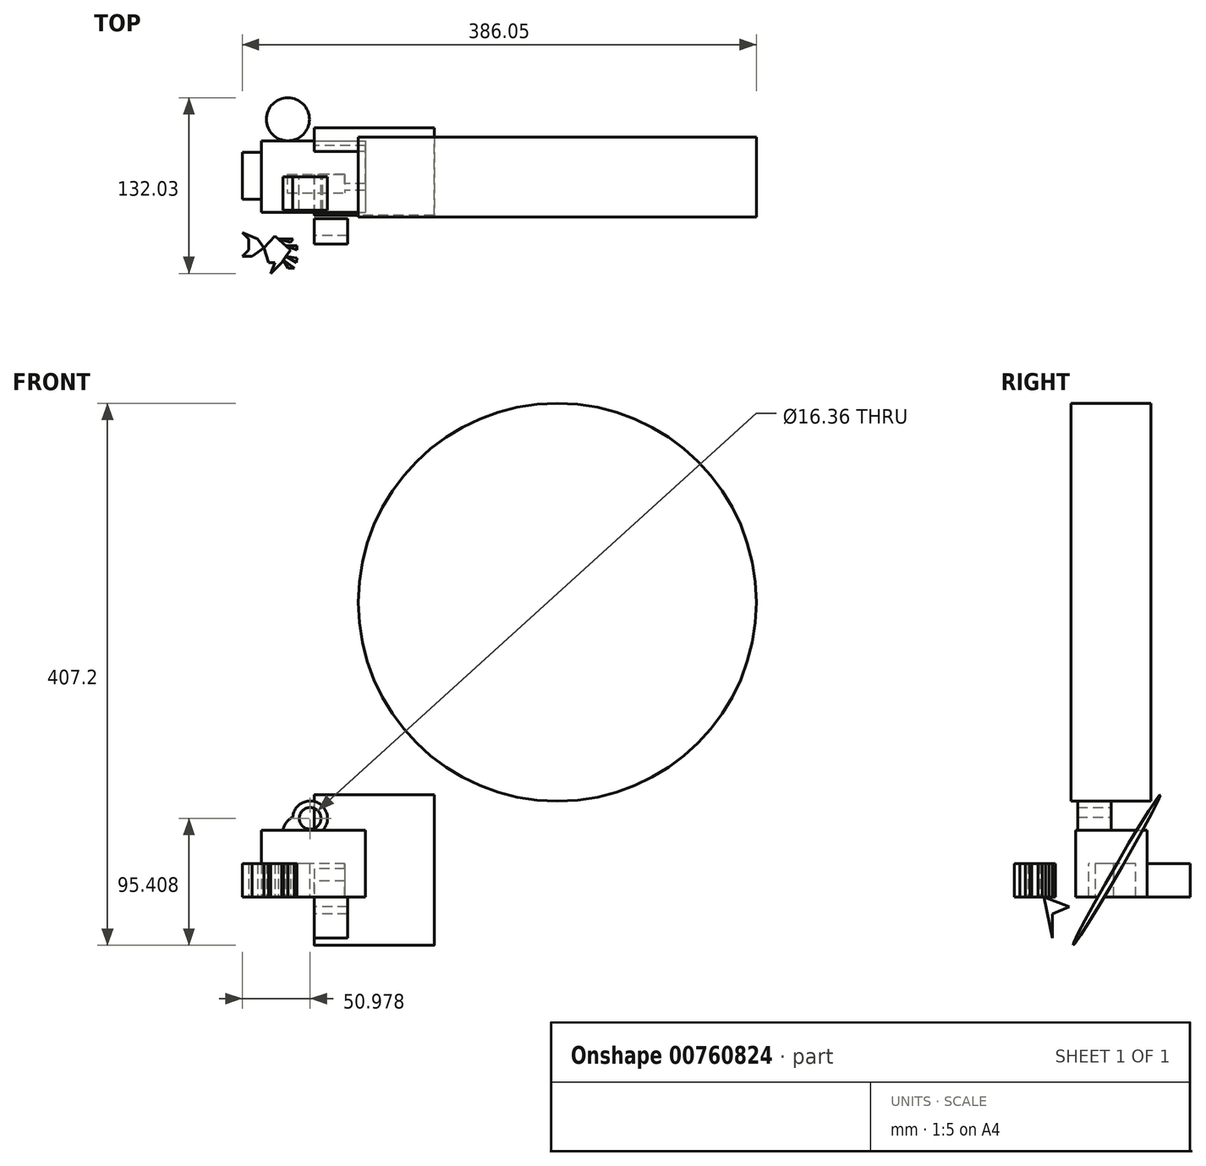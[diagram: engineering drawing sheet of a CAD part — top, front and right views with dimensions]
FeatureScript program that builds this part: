
annotation { "Feature Type Name" : "Feature", "Feature Type Description" : "" }
export const myFeature = defineFeature(function(context is Context, id is Id, definition is map)
    precondition{}
    {
        {
            var Q0;
            Q0=qCreatedBy(makeId("Top.planeOp"),FACE);
            var sketch = newSketch(context, id + "F0", { "sketchPlane" : qUnion([Q0])});
            skLineSegment(sketch, "E0.bottom", {"start": v(-39.72, 27.05) * mm, "end": v(38.3, 27.05) * mm});
            skLineSegment(sketch, "E0.top", {"start": v(-39.72, -26.66) * mm, "end": v(38.3, -26.66) * mm});
            skLineSegment(sketch, "E0.left", {"start": v(-39.72, 27.05) * mm, "end": v(-39.72, -26.66) * mm});
            skLineSegment(sketch, "E0.right", {"start": v(38.3, 27.05) * mm, "end": v(38.3, -26.66) * mm});
            skSolve(sketch);
        }
        {
            var Q0;
            Q0 = qSketchRegion(id + "F0", true);
            extrude(context, id + "F1", {"entities" : qUnion([Q0]), "depth" : 50 * mm, "offsetDistance" : 25.4 * mm});
        }
        {
            var Q0;
            Q0=qCreatedBy(makeId("Top.planeOp"),FACE);
            var sketch = newSketch(context, id + "F2", { "sketchPlane" : qUnion([Q0])});
            skLineSegment(sketch, "E1.bottom", {"start": v(-20.39, 11.58) * mm, "end": v(22.9, 11.58) * mm});
            skLineSegment(sketch, "E1.top", {"start": v(-20.39, -11.8) * mm, "end": v(22.9, -11.8) * mm});
            skLineSegment(sketch, "E1.left", {"start": v(-20.39, 11.58) * mm, "end": v(-20.39, -11.8) * mm});
            skLineSegment(sketch, "E1.right", {"start": v(22.9, 11.58) * mm, "end": v(22.9, -11.8) * mm});
            skSolve(sketch);
        }
        {
            var Q0;
            Q0 = qSketchRegion(id + "F2", true);
            extrude(context, id + "F3", {"entities" : qUnion([Q0]), "operationType" : NewBodyOperationType.REMOVE, "depth" : 25 * mm, "offsetDistance" : 25.4 * mm});
        }
        {
            var Q0;
            Q0=qCreatedBy(makeId("Top.planeOp"),FACE);
            var sketch = newSketch(context, id + "F4", { "sketchPlane" : qUnion([Q0])});
            skCircle(sketch, "E2", {"center": v(-19.82, 43.36) * mm, "radius": 16.16 * mm});
            skSolve(sketch);
        }
        {
            var Q0;
            Q0=makeQuery(id+"F4.imprint","IMPRINT",FACE,{"disambiguationData":[TD([[makeQuery(id+"F4.imprint","IMPRINT",EDGE,{"derivedFrom":sQuery(id+"F4.wireOp",EDGE,"E2")}),1.0]])]});
            extrude(context, id + "F5", {"entities" : qUnion([Q0]), "depth" : 25 * mm, "offsetDistance" : 25 * mm});
        }
        {
            var Q0;
            Q0=qCreatedBy(makeId("Top.planeOp"),FACE);
            var sketch = newSketch(context, id + "F6", { "sketchPlane" : qUnion([Q0])});
            skLineSegment(sketch, "E3.bottom", {"start": v(-53.98, 18.41) * mm, "end": v(-24.24, 18.41) * mm});
            skLineSegment(sketch, "E3.top", {"start": v(-53.98, -16.71) * mm, "end": v(-24.24, -16.71) * mm});
            skLineSegment(sketch, "E3.left", {"start": v(-53.98, 18.41) * mm, "end": v(-53.98, -16.71) * mm});
            skLineSegment(sketch, "E3.right", {"start": v(-24.24, 18.41) * mm, "end": v(-24.24, -16.71) * mm});
            skSolve(sketch);
        }
        {
            var Q0;
            Q0=makeQuery(id+"F6.imprint","IMPRINT",FACE,{"disambiguationData":[TD([[makeQuery(id+"F6.imprint","IMPRINT",EDGE,{"derivedFrom":sQuery(id+"F6.wireOp",EDGE,"E3.bottom")}),-1.0]])]});
            extrude(context, id + "F7", {"entities" : qUnion([Q0]), "operationType" : NewBodyOperationType.ADD, "depth" : 25 * mm, "offsetDistance" : 25 * mm});
        }
        {
            var Q0;
            Q0=qCreatedBy(makeId("Front.planeOp"),FACE);
            var sketch = newSketch(context, id + "F8", { "sketchPlane" : qUnion([Q0])});
            skCircle(sketch, "E4", {"center": v(-3.15, 58.99) * mm, "radius": 13.07 * mm});
            skCircle(sketch, "E5", {"center": v(-3.15, 58.99) * mm, "radius": 8.18 * mm});
            skCircle(sketch, "E6", {"center": v(-10.15, 47.95) * mm, "radius": 13.46 * mm});
            skSolve(sketch);
        }
        {
            var Q0;
            Q0 = qSketchRegion(id + "F8", true);
            var Q1;
            Q1=makeQuery(id+"F1.opExtrude","SWEPT_FACE",FACE,{"disambiguationData":[OSD([sQuery(id+"F0.wireOp",EDGE,"E0.bottom")])]});
            extrude(context, id + "F9", {"entities" : qUnion([Q0, Q1]), "operationType" : NewBodyOperationType.ADD, "depth" : 25 * mm, "offsetDistance" : 25 * mm});
        }
        {
            var Q0;
            Q0=qCreatedBy(makeId("Right.planeOp"),FACE);
            var sketch = newSketch(context, id + "F10", { "sketchPlane" : qUnion([Q0])});
            skLineSegment(sketch, "E7", {"start": v(-43.98, -30.95) * mm, "end": v(-31.22, -9.08) * mm});
            skLineSegment(sketch, "E8", {"start": v(-31.22, -7.42) * mm, "end": v(-50.28, 0) * mm});
            skLineSegment(sketch, "E9", {"start": v(-43.98, -30.95) * mm, "end": v(-50.28, 0) * mm});
            skLineSegment(sketch, "E10", {"start": v(-31.22, -7.42) * mm, "end": v(-43.98, -12.66) * mm});
            skLineSegment(sketch, "E11", {"start": v(-43.98, -12.66) * mm, "end": v(-43.98, -30.95) * mm});
            skLineSegment(sketch, "E12", {"start": v(-43.98, -12.66) * mm, "end": v(-50.28, 0) * mm});
            skSolve(sketch);
        }
        {
            var Q0;
            Q0 = qSketchRegion(id + "F10", true);
            extrude(context, id + "F11", {"entities" : qUnion([Q0]), "depth" : 25 * mm, "offsetDistance" : 25 * mm});
        }
        {
            var Q0;
            Q0=qCreatedBy(makeId("Top.planeOp"),FACE);
            var sketch = newSketch(context, id + "F12", { "sketchPlane" : qUnion([Q0])});
            skLineSegment(sketch, "E13", {"start": v(-54.13, -41.87) * mm, "end": v(-49.15, -46.46) * mm});
            skLineSegment(sketch, "E14", {"start": v(-49.15, -46.46) * mm, "end": v(-49.15, -54.9) * mm});
            skLineSegment(sketch, "E15", {"start": v(-49.15, -54.9) * mm, "end": v(-54.13, -59.5) * mm});
            skLineSegment(sketch, "E16", {"start": v(-54.13, -59.5) * mm, "end": v(-46.85, -59.5) * mm});
            skLineSegment(sketch, "E17", {"start": v(-46.85, -59.5) * mm, "end": v(-37.84, -53.17) * mm});
            skLineSegment(sketch, "E18", {"start": v(-37.84, -53.17) * mm, "end": v(-42.55, -46.46) * mm});
            skLineSegment(sketch, "E19", {"start": v(-42.55, -46.46) * mm, "end": v(-54.13, -41.87) * mm});
            skLineSegment(sketch, "E20", {"start": v(-37.84, -53.17) * mm, "end": v(-29.53, -44.17) * mm});
            skPoint(sketch, "E20.endSnap0", {"position": v(-48.34, -44.17) * mm});
            skLineSegment(sketch, "E21", {"start": v(-29.53, -44.17) * mm, "end": v(-17.9, -54.9) * mm});
            skLineSegment(sketch, "E22", {"start": v(-17.9, -54.9) * mm, "end": v(-24.62, -64.28) * mm});
            skLineSegment(sketch, "E23", {"start": v(-24.62, -64.28) * mm, "end": v(-34.2, -64.28) * mm});
            skLineSegment(sketch, "E24", {"start": v(-34.2, -64.28) * mm, "end": v(-37.84, -53.17) * mm});
            skLineSegment(sketch, "E25", {"start": v(-29.53, -64.28) * mm, "end": v(-32.8, -72.5) * mm});
            skLineSegment(sketch, "E26", {"start": v(-32.8, -72.5) * mm, "end": v(-24.62, -64.28) * mm});
            skLineSegment(sketch, "E27", {"start": v(-27.04, -46.46) * mm, "end": v(-16, -46.46) * mm});
            skLineSegment(sketch, "E28", {"start": v(-16, -46.46) * mm, "end": v(-17.9, -49.13) * mm});
            skLineSegment(sketch, "E29", {"start": v(-17.9, -49.13) * mm, "end": v(-27.04, -46.46) * mm});
            skLineSegment(sketch, "E30", {"start": v(-21.6, -51.48) * mm, "end": v(-12.93, -51.48) * mm});
            skLineSegment(sketch, "E31", {"start": v(-12.93, -51.48) * mm, "end": v(-12.93, -54.9) * mm});
            skLineSegment(sketch, "E32", {"start": v(-12.93, -54.9) * mm, "end": v(-21.6, -51.48) * mm});
            skLineSegment(sketch, "E33", {"start": v(-21.6, -59.5) * mm, "end": v(-12.93, -60.83) * mm});
            skLineSegment(sketch, "E34", {"start": v(-12.93, -60.83) * mm, "end": v(-13.47, -64.28) * mm});
            skLineSegment(sketch, "E35", {"start": v(-13.47, -64.28) * mm, "end": v(-21.6, -59.5) * mm});
            skLineSegment(sketch, "E36", {"start": v(-23.35, -62.5) * mm, "end": v(-14.91, -68.55) * mm});
            skLineSegment(sketch, "E37", {"start": v(-14.91, -68.55) * mm, "end": v(-19.83, -68.55) * mm});
            skLineSegment(sketch, "E38", {"start": v(-19.83, -68.55) * mm, "end": v(-23.35, -62.5) * mm});
            skSolve(sketch);
        }
        {
            var Q0;
            Q0 = qSketchRegion(id + "F12", true);
            extrude(context, id + "F13", {"entities" : qUnion([Q0]), "depth" : 25 * mm, "offsetDistance" : 25 * mm});
        }
        {
            var Q0;
            Q0=qCreatedBy(makeId("Right.planeOp"),FACE);
            var sketch = newSketch(context, id + "F14", { "sketchPlane" : qUnion([Q0])});
            skEllipse(sketch, "E39", {"center": v(4.15, 20.12) * mm, "majorRadius": 65.34 * mm, "minorRadius": 2.27 * mm, "majorAxis": v(-0.5, -0.87)});
            skSolve(sketch);
        }
        {
            var Q0;
            Q0 = qSketchRegion(id + "F14", true);
            extrude(context, id + "F15", {"entities" : qUnion([Q0]), "operationType" : NewBodyOperationType.ADD, "depth" : 90 * mm, "offsetDistance" : 25 * mm});
        }
        {
            var Q0;
            Q0=qCreatedBy(makeId("Front.planeOp"),FACE);
            var sketch = newSketch(context, id + "F16", { "sketchPlane" : qUnion([Q0])});
            skCircle(sketch, "E40", {"center": v(182.49, 221.35) * mm, "radius": 149.44 * mm});
            skSolve(sketch);
        }
        {
            var Q0;
            Q0=makeQuery(id+"F16.imprint","IMPRINT",FACE,{"disambiguationData":[TD([[makeQuery(id+"F16.imprint","IMPRINT",EDGE,{"derivedFrom":sQuery(id+"F16.wireOp",EDGE,"E40")}),1.0]])]});
            extrude(context, id + "F17", {"entities" : qUnion([Q0]), "endBound" : BoundingType.SYMMETRIC, "depth" : 60 * mm, "offsetDistance" : 25 * mm});
        }
        {
            var Q0;
            Q0=makeQuery(id+"F17.opExtrude","CAP_FACE",FACE,{"disambiguationData":[OSD([sQuery(id+"F16.wireOp",EDGE,"E40")])],"isStart":false});
            var sketch = newSketch(context, id + "F18", { "sketchPlane" : qUnion([Q0])});
            skLineSegment(sketch, "E41", {"start": v(93.9, 165.12) * mm, "end": v(124.33, 330.52) * mm});
            skLineSegment(sketch, "E42", {"start": v(124.33, 330.52) * mm, "end": v(245.72, 281.34) * mm});
            skLineSegment(sketch, "E43", {"start": v(245.72, 281.34) * mm, "end": v(222.38, 127.05) * mm});
            skLineSegment(sketch, "E44", {"start": v(222.38, 127.05) * mm, "end": v(93.9, 165.12) * mm});
            skSolve(sketch);
        }
        {
            var Q0;
            Q0 = qSketchRegion(id + "F18", true);
            extrude(context, id + "F19", {"entities" : qUnion([Q0]), "operationType" : NewBodyOperationType.ADD, "oppositeDirection" : true, "depth" : 30 * mm, "offsetDistance" : 25 * mm});
        }
    });
